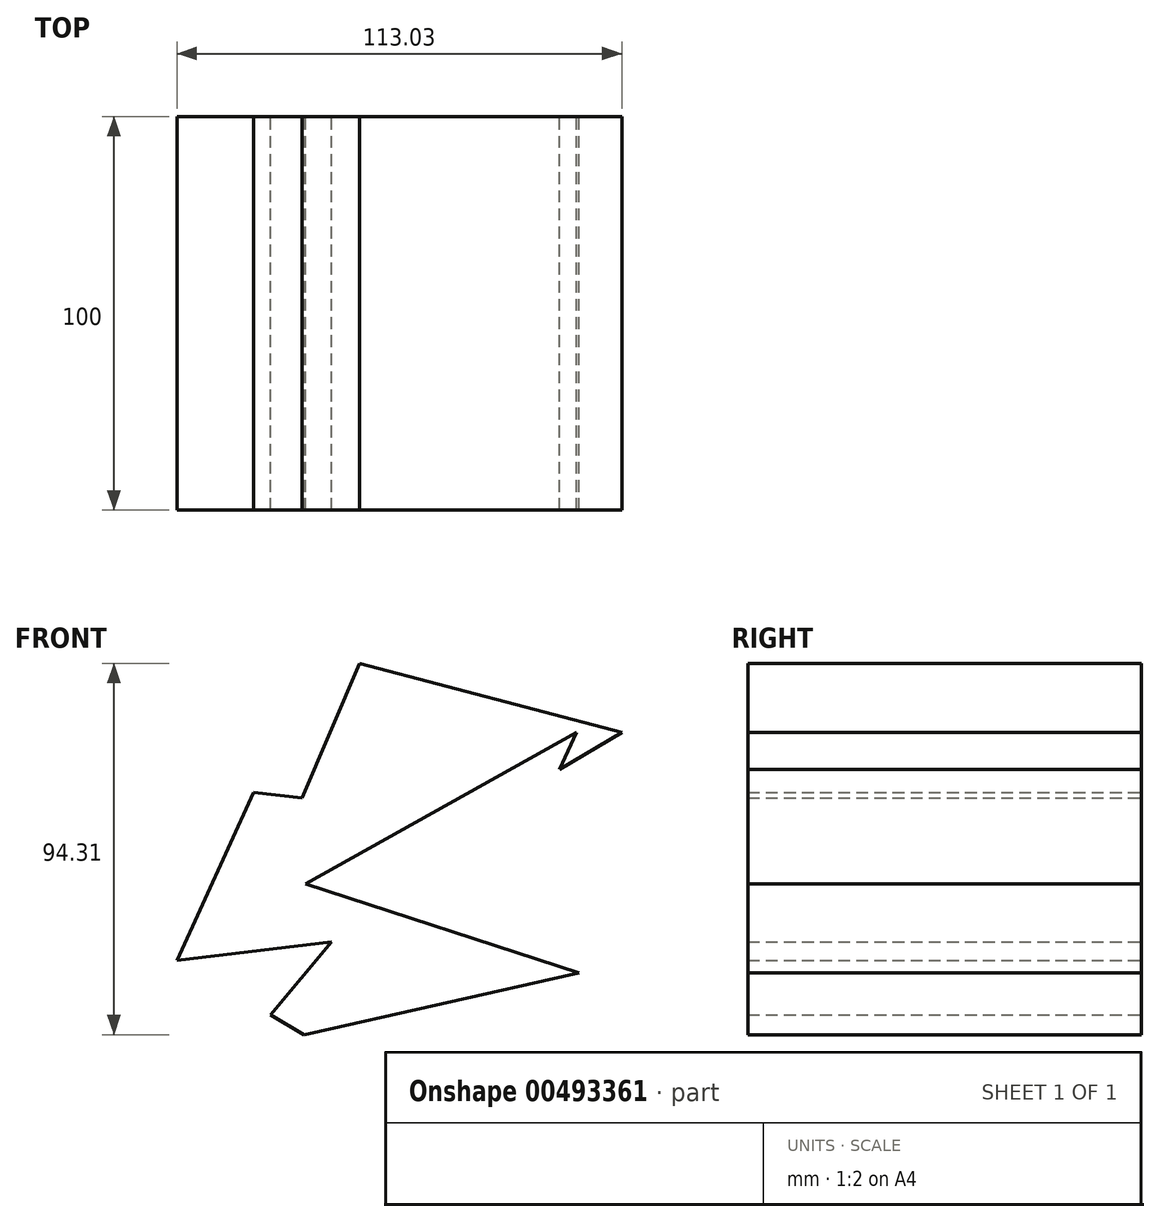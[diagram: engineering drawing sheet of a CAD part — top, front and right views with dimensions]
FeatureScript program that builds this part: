
annotation { "Feature Type Name" : "Feature", "Feature Type Description" : "" }
export const myFeature = defineFeature(function(context is Context, id is Id, definition is map)
    precondition{}
    {
        {
            var Q0;
            Q0=qCreatedBy(makeId("Front.planeOp"),FACE);
            var sketch = newSketch(context, id + "F0", { "sketchPlane" : qUnion([Q0])});
            skLineSegment(sketch, "E0", {"start": v(-19.8, 38.01) * mm, "end": v(-39.3, -4.73) * mm});
            skLineSegment(sketch, "E1", {"start": v(-39.3, -4.73) * mm, "end": v(22.1, -40.6) * mm});
            skLineSegment(sketch, "E2", {"start": v(-6.6, 14.77) * mm, "end": v(62.25, 53.22) * mm});
            skLineSegment(sketch, "E3", {"start": v(62.25, 53.22) * mm, "end": v(57.95, 43.75) * mm});
            skLineSegment(sketch, "E4", {"start": v(57.95, 43.75) * mm, "end": v(73.73, 53.22) * mm});
            skLineSegment(sketch, "E5", {"start": v(73.73, 53.22) * mm, "end": v(7.17, 70.72) * mm});
            skLineSegment(sketch, "E6", {"start": v(7.17, 70.72) * mm, "end": v(-7.46, 36.58) * mm});
            skLineSegment(sketch, "E7", {"start": v(-7.46, 36.58) * mm, "end": v(-19.8, 38.01) * mm});
            skLineSegment(sketch, "E8", {"start": v(-6.6, 14.77) * mm, "end": v(62.83, -7.89) * mm});
            skLineSegment(sketch, "E9", {"start": v(62.83, -7.89) * mm, "end": v(-22.66, -27.11) * mm});
            skLineSegment(sketch, "E10", {"start": v(-22.66, -27.11) * mm, "end": v(0, 0) * mm});
            skLineSegment(sketch, "E11", {"start": v(-39.3, -4.73) * mm, "end": v(0, 0) * mm});
            skSolve(sketch);
        }
        {
            var Q0;
            Q0=makeQuery(id+"F0.imprint","IMPRINT",FACE,{"disambiguationData":[TD([[makeQuery(id+"F0.imprint","IMPRINT",EDGE,{"derivedFrom":sQuery(id+"F0.wireOp",EDGE,"E0")}),1.0]])]});
            extrude(context, id + "F1", {"entities" : qUnion([Q0]), "depth" : 100 * mm});
        }
    });
